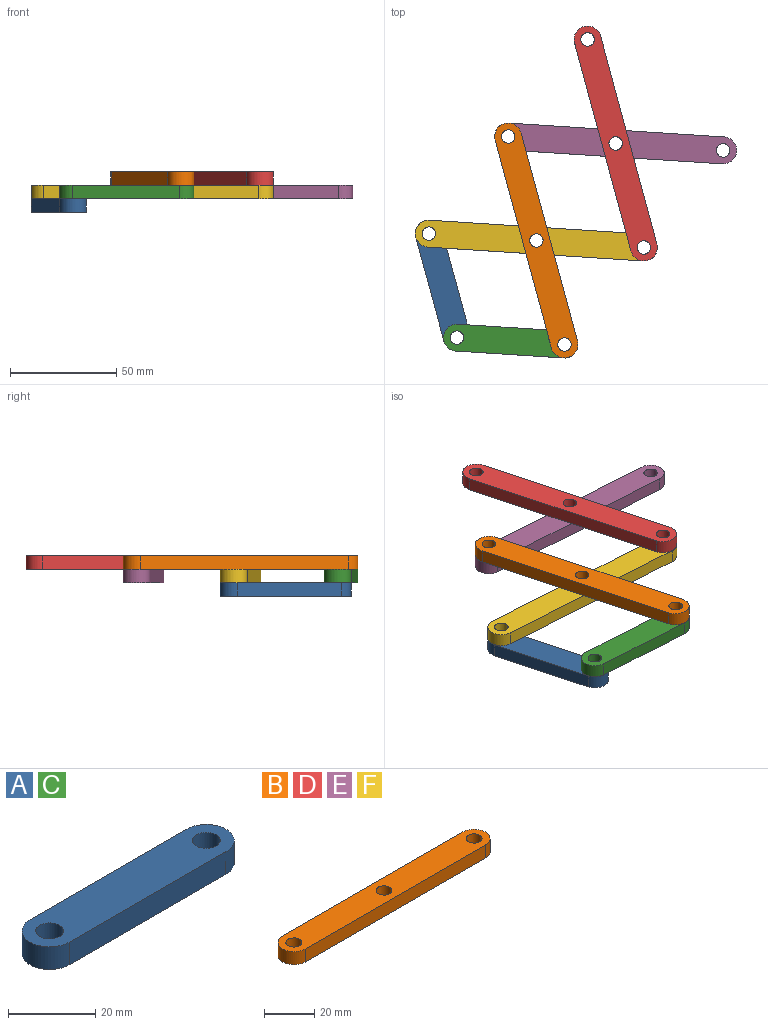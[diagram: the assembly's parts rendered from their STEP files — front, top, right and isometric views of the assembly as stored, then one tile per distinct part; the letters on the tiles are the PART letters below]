
ASSEMBLY  parts=6 mates=7
PART A: 8 faces, bbox 63.5x12.7x6.4 mm
  f0: cylinder r=6.35mm len=12.7mm, axis (0,0,-1), area 126.7mm2, adj f1,f3,f6,f7
  f1: plane 50.8x6.35mm, normal (0,-1,0), area 322.6mm2, adj f0,f2,f6,f7
  f2: cylinder r=6.35mm len=12.7mm, axis (0,0,-1), area 126.7mm2, adj f1,f3,f6,f7
  f3: plane 50.8x6.35mm, normal (0,1,0), area 322.6mm2, adj f0,f2,f6,f7
  f4: cylinder r=3.17mm len=6.35mm, axis (0,0,-1), area 126.7mm2, adj f6,f7
  f5: cylinder r=3.17mm len=6.35mm, axis (0,0,-1), area 126.7mm2, adj f6,f7
  f6: plane 63.5x12.7mm, normal (0,0,1), area 708.5mm2, adj f0,f1,f2,f3,f4,f5
  f7: plane 63.5x12.7mm, normal (0,0,-1), area 708.5mm2, adj f0,f1,f2,f3,f4,f5
PART B: 9 faces, bbox 114.3x12.7x6.4 mm
  f0: plane 101.6x6.35mm, normal (0,-1,0), area 645.2mm2, adj f1,f5,f7,f8
  f1: cylinder r=6.35mm len=12.7mm, axis (0,0,-1), area 126.7mm2, adj f0,f2,f7,f8
  f2: plane 101.6x6.35mm, normal (0,1,0), area 645.2mm2, adj f1,f5,f7,f8
  f3: cylinder r=3.17mm len=6.35mm, axis (0,0,-1), area 126.7mm2, adj f7,f8
  f4: cylinder r=3.17mm len=6.35mm, axis (0,0,-1), area 126.7mm2, adj f7,f8
  f5: cylinder r=6.35mm len=12.7mm, axis (0,0,-1), area 126.7mm2, adj f0,f2,f7,f8
  f6: cylinder r=3.17mm len=6.35mm, axis (0,0,-1), area 126.7mm2, adj f7,f8
  f7: plane 114.3x12.7mm, normal (0,0,1), area 1322mm2, adj f0,f1,f2,f3,f4,f5,f6
  f8: plane 114.3x12.7mm, normal (0,0,-1), area 1322mm2, adj f0,f1,f2,f3,f4,f5,f6
PART C: same geometry as A
PART D: same geometry as B
PART E: same geometry as B
PART F: same geometry as B
PLACE A rot(axis=(0,0,1),105.1deg) t=(2.91,13.56,0)mm
PLACE B rot(axis=(0,0,1),105.1deg) t=(18.67,39.44,12.7)mm
PLACE C rot(axis=(0,0,-1),3.7deg) t=(11.9,-7.13,6.35)mm
PLACE D rot(axis=(0,0,1),105.1deg) t=(56.1,85.21,12.7)mm
PLACE E rot(axis=(0,0,-1),3.7deg) t=(74.94,111.36,6.35)mm
PLACE F rot(axis=(0,0,-1),3.7deg) t=(37.5,65.59,6.35)mm
MATE revolute C.f2 <-> B.f4  axis (0,0,1) through (50.69,-3.27,12.7)mm
MATE revolute B.f6 <-> F.f6  axis (0,0,-1) through (37.44,45.77,12.7)mm
MATE revolute F.f1 <-> D.f4  axis (0,0,1) through (88.13,42.51,12.7)mm
MATE revolute E.f6 <-> D.f6  axis (0,0,1) through (74.88,91.55,12.7)mm
MATE revolute A.f0 <-> C.f0  axis (0,0,1) through (0,0,6.35)mm
MATE revolute A.f2 <-> F.f4  axis (0,0,1) through (-13.25,49.04,6.35)mm
MATE revolute B.f1 <-> E.f4  axis (0,0,-1) through (24.19,94.81,12.7)mm
